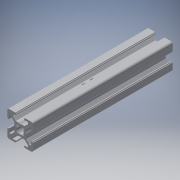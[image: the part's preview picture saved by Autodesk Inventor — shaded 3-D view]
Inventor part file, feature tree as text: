
AUTODESK INVENTOR PART (.ipt)
format: ipt  version: 2016 (Build 200138000, 138)  size: 414,208 bytes
history: native  units: in
note: dims shown in document units (in); Inventor stores cm internally (conversion verified against a paired STEP export)
features: other x3, sketch x2, extrude x1, hole x1, mirror x1
ambient origin geometry x8: Origin, YZ Plane, XZ Plane, XY Plane, X Axis, Y Axis, Z Axis, Center Point
bodies: Solid1 (feature_tree)
feature tree (8):
  other  "Blocks"
  extrude  "Extrusion1"  Depth=2.0in
  hole  "Hole1"  [1 undecoded]
  mirror  "Mirror1"
  sketch  "Sketch1"  dims[d1=0.0in d5=2.0in]
  other  "20x20"
  sketch  "Sketch3"  dims[d6=0.187in d7=0.75in d8=0.375in d9=0.25in d10=0.5635in d11=1.0in d12=0.8108in d13=1.0in d14=1.0in]
  other  "20x20:1"
note: 1 required parameter value undecoded (feature->parameter linkage not recoverable at this tier; creation-order binding heuristic only, values carry confidence <= 0.55)
